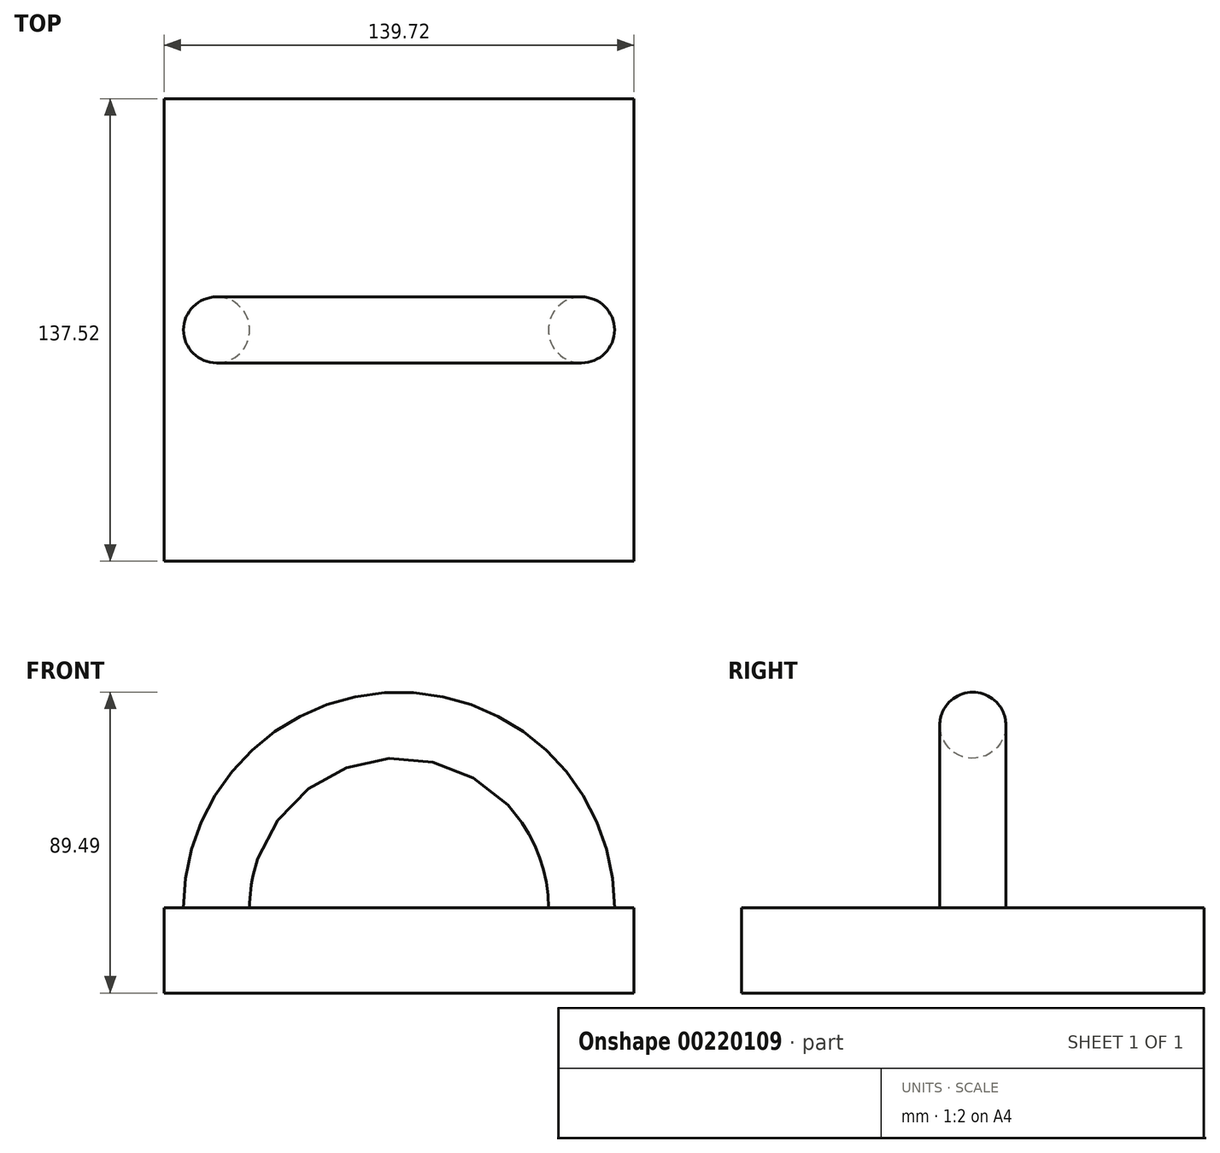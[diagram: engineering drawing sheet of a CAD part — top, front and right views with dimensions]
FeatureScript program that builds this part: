
annotation { "Feature Type Name" : "Feature", "Feature Type Description" : "" }
export const myFeature = defineFeature(function(context is Context, id is Id, definition is map)
    precondition{}
    {
        {
            var Q0;
            Q0=qCreatedBy(makeId("Top.planeOp"),FACE);
            var sketch = newSketch(context, id + "F0", { "sketchPlane" : qUnion([Q0])});
            skLineSegment(sketch, "E0.bottom", {"start": v(69.86, -68.76) * mm, "end": v(-69.86, -68.76) * mm});
            skLineSegment(sketch, "E0.top", {"start": v(69.86, 68.76) * mm, "end": v(-69.86, 68.76) * mm});
            skLineSegment(sketch, "E0.left", {"start": v(69.86, -68.76) * mm, "end": v(69.86, 68.76) * mm});
            skLineSegment(sketch, "E0.right", {"start": v(-69.86, -68.76) * mm, "end": v(-69.86, 68.76) * mm});
            skPoint(sketch, "E0.middle", {"position": v(0, 0) * mm});
            skLineSegment(sketch, "E1", {"start": v(0, 68.76) * mm, "end": v(0, -68.76) * mm});
            skSolve(sketch);
        }
        {
            var Q0;
            Q0=qCreatedBy(makeId("Top.planeOp"),FACE);
            var sketch = newSketch(context, id + "F1", { "sketchPlane" : qUnion([Q0])});
            skCircle(sketch, "E2", {"center": v(54.26, 0) * mm, "radius": 9.82 * mm});
            skSolve(sketch);
        }
        {
            var Q0;
            Q0 = qSketchRegion(id + "F0", true);
            extrude(context, id + "F2", {"entities" : qUnion([Q0]), "oppositeDirection" : true, "depth" : 25.4 * mm});
        }
        {
            var Q0;
            Q0 = qSketchRegion(id + "F1", true);
            var Q1;
            Q1=sQuery(id+"F0.wireOp",EDGE,"E1");
            revolve(context, id + "F3", {"entities" : qUnion([Q0]), "axis" : qUnion([Q1]), "revolveType" : RevolveType.ONE_DIRECTION, "angle" : 180 * degree});
        }
    });
